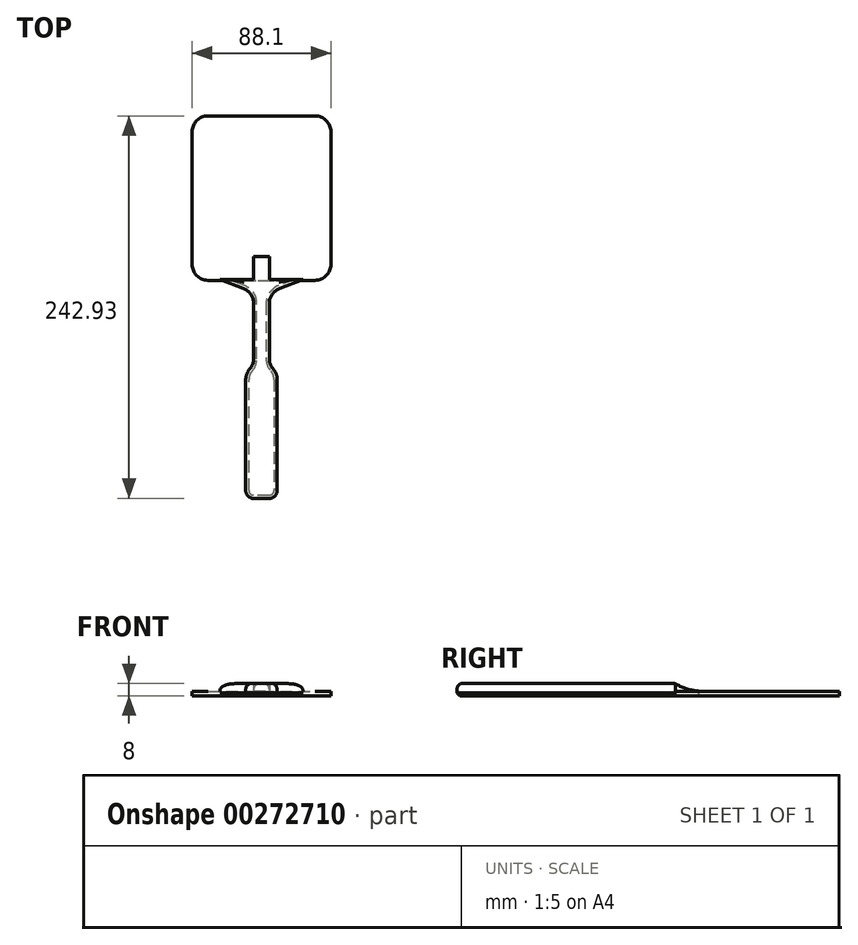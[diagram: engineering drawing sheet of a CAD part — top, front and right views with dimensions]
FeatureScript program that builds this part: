
annotation { "Feature Type Name" : "Feature", "Feature Type Description" : "" }
export const myFeature = defineFeature(function(context is Context, id is Id, definition is map)
    precondition{}
    {
        {
            var Q0;
            Q0=qCreatedBy(makeId("Top.planeOp"),FACE);
            var sketch = newSketch(context, id + "F0", { "sketchPlane" : qUnion([Q0])});
            skLineSegment(sketch, "E0", {"start": v(0, 148.5) * mm, "end": v(-148.5, 0) * mm, "construction": true});
            skLineSegment(sketch, "E1", {"start": v(-148.5, 0) * mm, "end": v(0, -148.5) * mm, "construction": true});
            skLineSegment(sketch, "E2", {"start": v(0, -148.5) * mm, "end": v(148.5, 0) * mm, "construction": true});
            skLineSegment(sketch, "E3", {"start": v(148.5, 0) * mm, "end": v(0, 148.5) * mm, "construction": true});
            skLineSegment(sketch, "E4.bottom", {"start": v(-34.05, 104.44) * mm, "end": v(34.05, 104.44) * mm});
            skLineSegment(sketch, "E4.top", {"start": v(-34.05, 0) * mm, "end": v(34.05, 0) * mm});
            skLineSegment(sketch, "E4.left", {"start": v(-44.05, 94.44) * mm, "end": v(-44.05, 10) * mm});
            skLineSegment(sketch, "E4.right", {"start": v(44.05, 94.44) * mm, "end": v(44.05, 10) * mm});
            skPoint(sketch, "E5.visualSharp", {"position": v(-44.05, 0) * mm});
            skArc(sketch, "E5.filletArc", {"start": v(-44.05, 10) * mm, "mid": v(-41.12, 2.93) * mm, "end": v(-34.05, 0) * mm});
            skPoint(sketch, "E6.visualSharp", {"position": v(44.05, 0) * mm});
            skArc(sketch, "E6.filletArc", {"start": v(34.05, 0) * mm, "mid": v(41.12, 2.93) * mm, "end": v(44.05, 10) * mm});
            skPoint(sketch, "E7.visualSharp", {"position": v(44.05, 104.44) * mm});
            skArc(sketch, "E7.filletArc", {"start": v(44.05, 94.44) * mm, "mid": v(41.12, 101.51) * mm, "end": v(34.05, 104.44) * mm});
            skPoint(sketch, "E8.visualSharp", {"position": v(-44.05, 104.44) * mm});
            skArc(sketch, "E8.filletArc", {"start": v(-34.05, 104.44) * mm, "mid": v(-41.12, 101.51) * mm, "end": v(-44.05, 94.44) * mm});
            skSolve(sketch);
        }
        {
            var Q0;
            Q0=qCreatedBy(makeId("Top.planeOp"),FACE);
            var sketch = newSketch(context, id + "F1", { "sketchPlane" : qUnion([Q0])});
            skLineSegment(sketch, "E9.bottom", {"start": v(-5, 15) * mm, "end": v(5, 15) * mm});
            skLineSegment(sketch, "E9.top", {"start": v(-5, -58.5) * mm, "end": v(5, -58.5) * mm});
            skLineSegment(sketch, "E9.left", {"start": v(-5, 15) * mm, "end": v(-5, -58.5) * mm});
            skLineSegment(sketch, "E9.right", {"start": v(5, 15) * mm, "end": v(5, -58.5) * mm});
            skLineSegment(sketch, "E10.bottom", {"start": v(-10, -138.5) * mm, "end": v(10, -138.5) * mm});
            skLineSegment(sketch, "E10.top", {"start": v(-10, -58.5) * mm, "end": v(10, -58.5) * mm});
            skLineSegment(sketch, "E10.left", {"start": v(-10, -138.5) * mm, "end": v(-10, -58.5) * mm});
            skLineSegment(sketch, "E10.right", {"start": v(10, -138.5) * mm, "end": v(10, -58.5) * mm});
            skLineSegment(sketch, "E11", {"start": v(-26.22, 0.4) * mm, "end": v(-5, -7.71) * mm});
            skLineSegment(sketch, "E12", {"start": v(-5, -7.71) * mm, "end": v(5, -7.71) * mm});
            skLineSegment(sketch, "E13", {"start": v(5, -7.71) * mm, "end": v(26.22, 0.4) * mm});
            skLineSegment(sketch, "E14", {"start": v(26.22, 0.4) * mm, "end": v(-26.22, 0.4) * mm});
            skLineSegment(sketch, "E15.bottom", {"start": v(-26.22, 0.4) * mm, "end": v(-21.22, 0.4) * mm});
            skLineSegment(sketch, "E15.top", {"start": v(-26.22, 5.4) * mm, "end": v(-21.22, 5.4) * mm});
            skLineSegment(sketch, "E15.left", {"start": v(-26.22, 0.4) * mm, "end": v(-26.22, 5.4) * mm});
            skLineSegment(sketch, "E15.right", {"start": v(-21.22, 0.4) * mm, "end": v(-21.22, 5.4) * mm});
            skLineSegment(sketch, "E16.bottom", {"start": v(26.22, 0.4) * mm, "end": v(21.22, 0.4) * mm});
            skLineSegment(sketch, "E16.top", {"start": v(26.22, 5.4) * mm, "end": v(21.22, 5.4) * mm});
            skLineSegment(sketch, "E16.left", {"start": v(26.22, 0.4) * mm, "end": v(26.22, 5.4) * mm});
            skLineSegment(sketch, "E16.right", {"start": v(21.22, 0.4) * mm, "end": v(21.22, 5.4) * mm});
            skSolve(sketch);
        }
        {
            var Q0;
            Q0=makeQuery(id+"F0.imprint","IMPRINT",FACE,{"disambiguationData":[TD([[makeQuery(id+"F0.imprint","IMPRINT",EDGE,{"derivedFrom":sQuery(id+"F0.wireOp",EDGE,"E4.bottom")}),-1.0]])]});
            extrude(context, id + "F2", {"entities" : qUnion([Q0]), "depth" : 3 * mm});
        }
        {
            var Q0;
            Q0=makeQuery(id+"F1.imprint","IMPRINT",FACE,{"disambiguationData":[TD([[makeQuery(id+"F1.imprint","IMPRINT",EDGE,{"derivedFrom":sQuery(id+"F1.wireOp",EDGE,"E10.bottom")}),1.0]])]});
            var Q1;
            {var subQ3=sQuery(id+"F1.wireOp",EDGE,"E12");Q1=makeQuery(id+"F1.imprint","IMPRINT",FACE,{"disambiguationData":[TD([[makeQuery(id+"F1.imprint","IMPRINT",EDGE,{"derivedFrom":subQ3}),-1.0]])]});}
            var Q2;
            {var subQ0=sQuery(id+"F1.wireOp",EDGE,"E12");Q2=makeQuery(id+"F1.imprint","IMPRINT",FACE,{"disambiguationData":[TD([[makeQuery(id+"F1.imprint","IMPRINT",EDGE,{"derivedFrom":subQ0}),1.0]])]});}
            var Q3;
            {var subQ0=sQuery(id+"F1.wireOp",EDGE,"E11");Q3=makeQuery(id+"F1.imprint","IMPRINT",FACE,{"disambiguationData":[TD([[makeQuery(id+"F1.imprint","IMPRINT",EDGE,{"derivedFrom":subQ0}),1.0]])]});}
            var Q4;
            {var subQ0=sQuery(id+"F1.wireOp",EDGE,"E13");Q4=makeQuery(id+"F1.imprint","IMPRINT",FACE,{"disambiguationData":[TD([[makeQuery(id+"F1.imprint","IMPRINT",EDGE,{"derivedFrom":subQ0}),1.0]])]});}
            var Q5;
            {var subQ0=sQuery(id+"F1.wireOp",EDGE,"E9.bottom");Q5=makeQuery(id+"F1.imprint","IMPRINT",FACE,{"disambiguationData":[TD([[makeQuery(id+"F1.imprint","IMPRINT",EDGE,{"derivedFrom":subQ0}),-1.0]])]});}
            var Q6;
            Q6=makeQuery(id+"F1.imprint","IMPRINT",FACE,{"disambiguationData":[TD([[makeQuery(id+"F1.imprint","IMPRINT",EDGE,{"derivedFrom":sQuery(id+"F1.wireOp",EDGE,"E15.bottom")}),1.0]])]});
            var Q7;
            Q7=makeQuery(id+"F1.imprint","IMPRINT",FACE,{"disambiguationData":[TD([[makeQuery(id+"F1.imprint","IMPRINT",EDGE,{"derivedFrom":sQuery(id+"F1.wireOp",EDGE,"E16.bottom")}),-1.0]])]});
            extrude(context, id + "F3", {"entities" : qUnion([Q0, Q1, Q2, Q3, Q4, Q5, Q6, Q7]), "depth" : 8 * mm});
        }
        {
            var Q0;
            Q0=makeQuery(id+"F3.opExtrude","SWEPT_EDGE",EDGE,{"disambiguationData":[OSD([sQuery(id+"F1.wireOp",EDGE,"E9.left"),sQuery(id+"F1.wireOp",EDGE,"E10.top")])]});
            var Q1;
            Q1=makeQuery(id+"F3.opExtrude","SWEPT_EDGE",EDGE,{"disambiguationData":[OSD([sQuery(id+"F1.wireOp",EDGE,"E9.right"),sQuery(id+"F1.wireOp",EDGE,"E10.top")])]});
            fillet(context, id + "F4", {"entities" : qUnion([Q0, Q1]), "radius" : 10 * mm, "tangentPropagation" : true, "allowEdgeOverflow" : false});
        }
        {
            var Q0;
            Q0=makeQuery(id+"F4.opFillet","BLEND_EDGE",EDGE,{"blendedFrom":[makeQuery(id+"F3.opExtrude","SWEPT_EDGE",EDGE,{"disambiguationData":[OSD([sQuery(id+"F1.wireOp",EDGE,"E9.right"),sQuery(id+"F1.wireOp",EDGE,"E10.top")])]}),makeQuery(id+"F3.opExtrude","SWEPT_FACE",FACE,{"disambiguationData":[OSD([sQuery(id+"F1.wireOp",EDGE,"E10.right")])]})],"blendedInto":[makeQuery(id+"F3.opExtrude","SWEPT_FACE",FACE,{"disambiguationData":[OSD([sQuery(id+"F1.wireOp",EDGE,"E10.right")])]})]});
            var Q1;
            Q1=makeQuery(id+"F4.opFillet","BLEND_EDGE",EDGE,{"blendedFrom":[makeQuery(id+"F3.opExtrude","SWEPT_EDGE",EDGE,{"disambiguationData":[OSD([sQuery(id+"F1.wireOp",EDGE,"E9.left"),sQuery(id+"F1.wireOp",EDGE,"E10.top")])]}),makeQuery(id+"F3.opExtrude","SWEPT_FACE",FACE,{"disambiguationData":[OSD([sQuery(id+"F1.wireOp",EDGE,"E10.left")])]})],"blendedInto":[makeQuery(id+"F3.opExtrude","SWEPT_FACE",FACE,{"disambiguationData":[OSD([sQuery(id+"F1.wireOp",EDGE,"E10.left")])]})]});
            fillet(context, id + "F5", {"entities" : qUnion([Q0, Q1]), "radius" : 10 * mm, "tangentPropagation" : true, "allowEdgeOverflow" : false});
        }
        {
            var Q0;
            Q0=makeQuery(id+"F3.opExtrude","SWEPT_EDGE",EDGE,{"disambiguationData":[OSD([sQuery(id+"F1.wireOp",EDGE,"E10.bottom"),sQuery(id+"F1.wireOp",EDGE,"E10.left")])]});
            var Q1;
            Q1=makeQuery(id+"F3.opExtrude","SWEPT_EDGE",EDGE,{"disambiguationData":[OSD([sQuery(id+"F1.wireOp",EDGE,"E10.bottom"),sQuery(id+"F1.wireOp",EDGE,"E10.right")])]});
            fillet(context, id + "F6", {"entities" : qUnion([Q0, Q1]), "radius" : 5 * mm, "tangentPropagation" : true, "allowEdgeOverflow" : false});
        }
        {
            var Q0;
            Q0=makeQuery(id+"F3.opExtrude","SWEPT_EDGE",EDGE,{"disambiguationData":[OSD([sQuery(id+"F1.wireOp",EDGE,"E9.left"),sQuery(id+"F1.wireOp",EDGE,"E11"),sQuery(id+"F1.wireOp",EDGE,"E12")])]});
            var Q1;
            Q1=makeQuery(id+"F3.opExtrude","SWEPT_EDGE",EDGE,{"disambiguationData":[OSD([sQuery(id+"F1.wireOp",EDGE,"E9.right"),sQuery(id+"F1.wireOp",EDGE,"E12"),sQuery(id+"F1.wireOp",EDGE,"E13")])]});
            fillet(context, id + "F7", {"entities" : qUnion([Q0, Q1]), "radius" : 10 * mm, "tangentPropagation" : true, "allowEdgeOverflow" : false});
        }
        {
            var Q0;
            Q0=qCreatedBy(makeId("Right.planeOp"),FACE);
            var sketch = newSketch(context, id + "F8", { "sketchPlane" : qUnion([Q0])});
            skCircle(sketch, "E17", {"center": v(17.17, 34.99) * mm, "radius": 31.99 * mm});
            skPoint(sketch, "E18", {"position": v(0, 8) * mm});
            skSolve(sketch);
        }
        {
            var Q0;
            Q0=makeQuery(id+"F8.imprint","IMPRINT",FACE,{"disambiguationData":[TD([[makeQuery(id+"F8.imprint","IMPRINT",EDGE,{"derivedFrom":sQuery(id+"F8.wireOp",EDGE,"E17")}),1.0]])]});
            extrude(context, id + "F9", {"entities" : qUnion([Q0]), "operationType" : NewBodyOperationType.REMOVE, "oppositeDirection" : true, "depth" : 30 * mm, "hasSecondDirection" : true, "secondDirectionOppositeDirection" : false, "secondDirectionDepth" : 30 * mm});
        }
        {
            var Q0;
            Q0=makeQuery(id+"F3.opExtrude","CAP_FACE",FACE,{"disambiguationData":[OSD([sQuery(id+"F1.wireOp",EDGE,"E9.bottom"),sQuery(id+"F1.wireOp",EDGE,"E9.left"),sQuery(id+"F1.wireOp",EDGE,"E9.right"),sQuery(id+"F1.wireOp",EDGE,"E10.bottom"),sQuery(id+"F1.wireOp",EDGE,"E10.top"),sQuery(id+"F1.wireOp",EDGE,"E10.left"),sQuery(id+"F1.wireOp",EDGE,"E10.right"),sQuery(id+"F1.wireOp",EDGE,"E11"),sQuery(id+"F1.wireOp",EDGE,"E13"),sQuery(id+"F1.wireOp",EDGE,"E14"),sQuery(id+"F1.wireOp",EDGE,"E15.top"),sQuery(id+"F1.wireOp",EDGE,"E15.left"),sQuery(id+"F1.wireOp",EDGE,"E15.right"),sQuery(id+"F1.wireOp",EDGE,"E16.top"),sQuery(id+"F1.wireOp",EDGE,"E16.left"),sQuery(id+"F1.wireOp",EDGE,"E16.right")])],"isStart":false});
            fillet(context, id + "F10", {"entities" : qUnion([Q0]), "radius" : 4 * mm, "tangentPropagation" : true, "allowEdgeOverflow" : false});
        }
        {
            var Q0;
            Q0=makeQuery(id+"F3.opExtrude","CAP_EDGE",EDGE,{"disambiguationData":[OSD([sQuery(id+"F1.wireOp",EDGE,"E10.left")])],"isStart":true});
            chamfer(context, id + "F11", {"entities" : qUnion([Q0]), "width" : 2 * mm, "tangentPropagation" : true});
        }
    });
